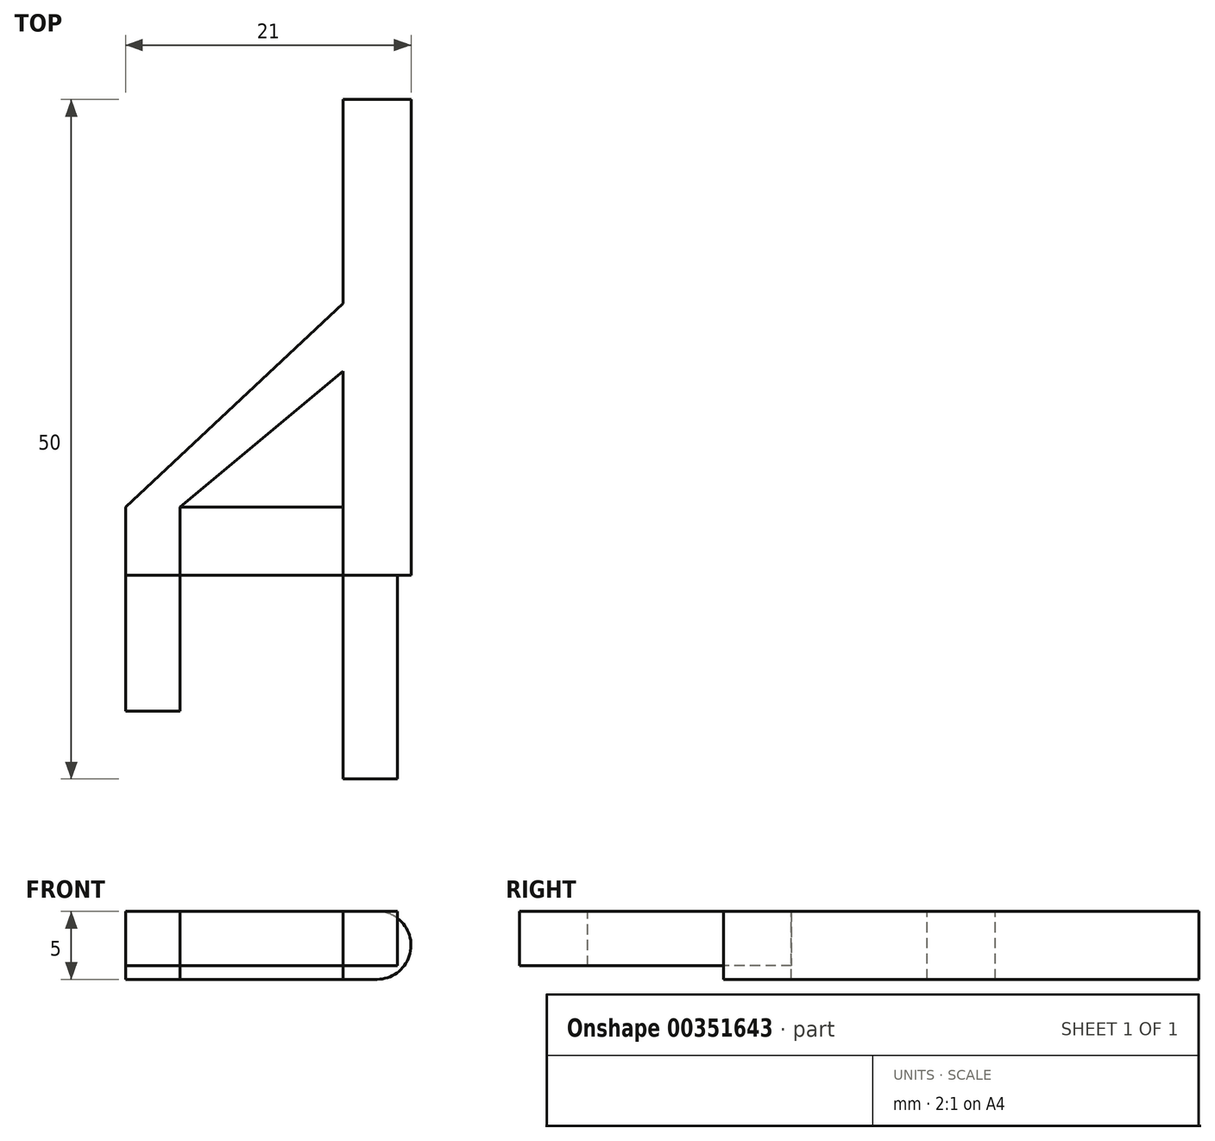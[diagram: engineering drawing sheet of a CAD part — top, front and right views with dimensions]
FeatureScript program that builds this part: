
annotation { "Feature Type Name" : "Feature", "Feature Type Description" : "" }
export const myFeature = defineFeature(function(context is Context, id is Id, definition is map)
    precondition{}
    {
        {
            var Q0;
            Q0=qCreatedBy(makeId("Front.planeOp"),FACE);
            var sketch = newSketch(context, id + "F0", { "sketchPlane" : qUnion([Q0])});
            skLineSegment(sketch, "E0.bottom", {"start": v(0, 0) * mm, "end": v(20, 0) * mm});
            skLineSegment(sketch, "E0.top", {"start": v(0, 4) * mm, "end": v(20, 4) * mm});
            skLineSegment(sketch, "E0.left", {"start": v(0, 0) * mm, "end": v(0, 4) * mm});
            skLineSegment(sketch, "E0.right", {"start": v(20, 0) * mm, "end": v(20, 4) * mm});
            skLineSegment(sketch, "E1", {"start": v(0, 4) * mm, "end": v(4, 4) * mm, "construction": true});
            skLineSegment(sketch, "E2", {"start": v(4, 4) * mm, "end": v(4, 0) * mm});
            skLineSegment(sketch, "E3", {"start": v(20, 4) * mm, "end": v(16, 4) * mm, "construction": true});
            skLineSegment(sketch, "E4", {"start": v(16, 4) * mm, "end": v(16, 0) * mm});
            skPoint(sketch, "E5", {"position": v(0, 4) * mm});
            skPoint(sketch, "E6", {"position": v(20, 4) * mm});
            skPoint(sketch, "E7", {"position": v(20, 0) * mm});
            skPoint(sketch, "E8", {"position": v(0, 0) * mm});
            skSolve(sketch);
        }
        {
            var Q0;
            {var subQ0=sQuery(id+"F0.wireOp",EDGE,"E0.left");Q0=makeQuery(id+"F0.imprint","IMPRINT",FACE,{"disambiguationData":[TD([[makeQuery(id+"F0.imprint","IMPRINT",EDGE,{"derivedFrom":subQ0}),-1.0]])]});}
            extrude(context, id + "F1", {"entities" : qUnion([Q0]), "depth" : 10 * mm});
        }
        {
            var Q0;
            {var subQ0=sQuery(id+"F0.wireOp",EDGE,"E0.right");Q0=makeQuery(id+"F0.imprint","IMPRINT",FACE,{"disambiguationData":[TD([[makeQuery(id+"F0.imprint","IMPRINT",EDGE,{"derivedFrom":subQ0}),1.0]])]});}
            extrude(context, id + "F2", {"entities" : qUnion([Q0]), "depth" : 15 * mm});
        }
        {
            var Q0;
            {var subQ0=sQuery(id+"F0.wireOp",EDGE,"E2");Q0=makeQuery(id+"F0.imprint","IMPRINT",FACE,{"disambiguationData":[TD([[makeQuery(id+"F0.imprint","IMPRINT",EDGE,{"derivedFrom":subQ0}),1.0]])]});}
            extrude(context, id + "F3", {"entities" : qUnion([Q0]), "depth" : -5 * mm});
        }
        {
            var Q0;
            Q0=makeQuery(id+"F3.opExtrude","SWEPT_FACE",FACE,{"disambiguationData":[OSD([sQuery(id+"F0.wireOp",EDGE,"E0.top")])]});
            var sketch = newSketch(context, id + "F4", { "sketchPlane" : qUnion([Q0])});
            skLineSegment(sketch, "E9.bottom", {"start": v(16, 5) * mm, "end": v(21, 5) * mm});
            skLineSegment(sketch, "E9.top", {"start": v(16, 0) * mm, "end": v(21, 0) * mm});
            skLineSegment(sketch, "E9.left", {"start": v(16, 5) * mm, "end": v(16, 0) * mm});
            skLineSegment(sketch, "E9.right", {"start": v(21, 5) * mm, "end": v(21, 0) * mm});
            skLineSegment(sketch, "E10", {"start": v(16, 5) * mm, "end": v(16, 35) * mm});
            skLineSegment(sketch, "E11", {"start": v(16, 35) * mm, "end": v(21, 35) * mm});
            skLineSegment(sketch, "E12", {"start": v(21, 35) * mm, "end": v(21, 5) * mm});
            skLineSegment(sketch, "E13", {"start": v(0, 0) * mm, "end": v(0, 5) * mm});
            skLineSegment(sketch, "E14", {"start": v(0, 5) * mm, "end": v(4, 5) * mm});
            skLineSegment(sketch, "E15", {"start": v(4, 5) * mm, "end": v(4, 0) * mm});
            skLineSegment(sketch, "E16", {"start": v(4, 0) * mm, "end": v(0, 0) * mm});
            skLineSegment(sketch, "E17", {"start": v(0, 5) * mm, "end": v(16, 20) * mm});
            skLineSegment(sketch, "E18", {"start": v(16, 20) * mm, "end": v(16, 15) * mm});
            skLineSegment(sketch, "E19", {"start": v(16, 15) * mm, "end": v(4, 5) * mm});
            skSolve(sketch);
        }
        {
            var Q0;
            {var subQ2=sQuery(id+"F4.wireOp",EDGE,"E9.bottom");Q0=makeQuery(id+"F4.imprint","IMPRINT",FACE,{"disambiguationData":[TD([[makeQuery(id+"F4.imprint","IMPRINT",EDGE,{"derivedFrom":subQ2}),1.0]])]});}
            var Q1;
            Q1=makeQuery(id+"F4.imprint","IMPRINT",FACE,{"disambiguationData":[TD([[makeQuery(id+"F4.imprint","IMPRINT",EDGE,{"derivedFrom":sQuery(id+"F4.wireOp",EDGE,"E13")}),-1.0]])]});
            var Q2;
            Q2=makeQuery(id+"F4.imprint","IMPRINT",FACE,{"disambiguationData":[TD([[makeQuery(id+"F4.imprint","IMPRINT",EDGE,{"derivedFrom":sQuery(id+"F4.wireOp",EDGE,"E14")}),1.0]])]});
            var Q3;
            Q3=makeQuery(id+"F4.imprint","IMPRINT",FACE,{"disambiguationData":[TD([[makeQuery(id+"F4.imprint","IMPRINT",EDGE,{"derivedFrom":sQuery(id+"F4.wireOp",EDGE,"E9.bottom")}),-1.0]])]});
            extrude(context, id + "F5", {"entities" : qUnion([Q0, Q1, Q2, Q3]), "depth" : -5 * mm});
        }
        {
            var Q0;
            Q0=makeQuery(id+"F5.opExtrude","CAP_EDGE",EDGE,{"disambiguationData":[OSD([sQuery(id+"F4.wireOp",EDGE,"E9.right"),sQuery(id+"F4.wireOp",EDGE,"E12")])],"isStart":false});
            var Q1;
            Q1=makeQuery(id+"F5.opExtrude","CAP_EDGE",EDGE,{"disambiguationData":[OSD([sQuery(id+"F4.wireOp",EDGE,"E9.right"),sQuery(id+"F4.wireOp",EDGE,"E12")])],"isStart":true});
            fillet(context, id + "F6", {"entities" : qUnion([Q0, Q1]), "radius" : 2.5 * mm, "tangentPropagation" : true, "allowEdgeOverflow" : false});
        }
    });
